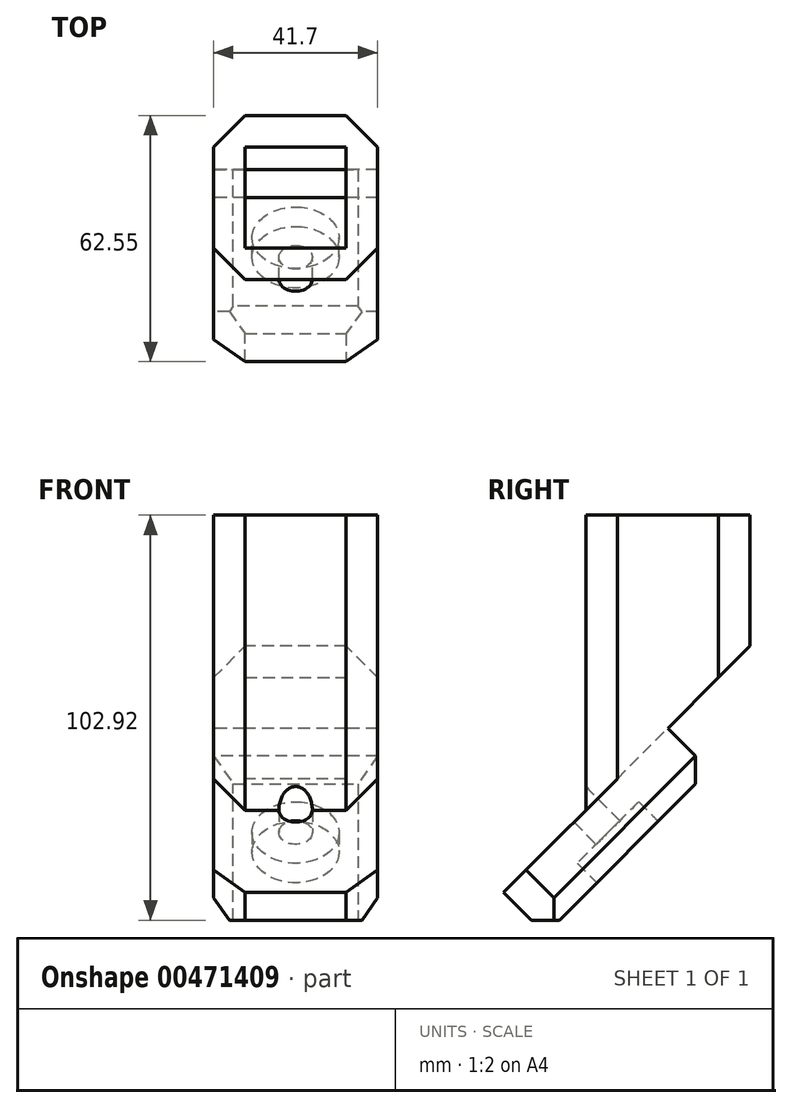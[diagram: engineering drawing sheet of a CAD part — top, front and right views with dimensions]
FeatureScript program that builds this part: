
annotation { "Feature Type Name" : "Feature", "Feature Type Description" : "" }
export const myFeature = defineFeature(function(context is Context, id is Id, definition is map)
    precondition{}
    {
        {
            var Q0;
            Q0=qCreatedBy(makeId("Top.planeOp"),FACE);
            var sketch = newSketch(context, id + "F0", { "sketchPlane" : qUnion([Q0])});
            skLineSegment(sketch, "E0", {"start": v(0, 0) * mm, "end": v(0, 12.85) * mm, "construction": true});
            skLineSegment(sketch, "E1", {"start": v(0, 12.85) * mm, "end": v(12.85, 12.85) * mm});
            skLineSegment(sketch, "E2", {"start": v(12.85, 12.85) * mm, "end": v(12.85, 0) * mm});
            skLineSegment(sketch, "E3", {"start": v(12.85, 0) * mm, "end": v(0, 0) * mm, "construction": true});
            skLineSegment(sketch, "E4", {"start": v(12.85, 0) * mm, "end": v(12.85, -12.85) * mm});
            skLineSegment(sketch, "E5", {"start": v(12.85, -12.85) * mm, "end": v(0, -12.85) * mm});
            skLineSegment(sketch, "E6", {"start": v(0, -12.85) * mm, "end": v(0, 0) * mm, "construction": true});
            skLineSegment(sketch, "E7", {"start": v(0, 0) * mm, "end": v(-12.85, 0) * mm, "construction": true});
            skLineSegment(sketch, "E8", {"start": v(-12.85, 0) * mm, "end": v(-12.85, 12.85) * mm});
            skLineSegment(sketch, "E9", {"start": v(-12.85, 12.85) * mm, "end": v(0, 12.85) * mm});
            skLineSegment(sketch, "E10", {"start": v(-12.85, 0) * mm, "end": v(-12.85, -12.85) * mm});
            skLineSegment(sketch, "E11", {"start": v(-12.85, -12.85) * mm, "end": v(0, -12.85) * mm});
            skLineSegment(sketch, "E12", {"start": v(0, 12.85) * mm, "end": v(0, 20.85) * mm, "construction": true});
            skLineSegment(sketch, "E13", {"start": v(0, 20.85) * mm, "end": v(20.85, 20.85) * mm});
            skLineSegment(sketch, "E14", {"start": v(20.85, 20.85) * mm, "end": v(20.85, 0) * mm});
            skLineSegment(sketch, "E15", {"start": v(20.85, 0) * mm, "end": v(12.85, 0) * mm, "construction": true});
            skLineSegment(sketch, "E16", {"start": v(20.85, 0) * mm, "end": v(20.85, -20.85) * mm});
            skLineSegment(sketch, "E17", {"start": v(20.85, -20.85) * mm, "end": v(0, -20.85) * mm});
            skLineSegment(sketch, "E18", {"start": v(0, -20.85) * mm, "end": v(0, -12.85) * mm, "construction": true});
            skLineSegment(sketch, "E19", {"start": v(0, -20.85) * mm, "end": v(-20.85, -20.85) * mm});
            skLineSegment(sketch, "E20", {"start": v(-20.85, -20.85) * mm, "end": v(-20.85, 0) * mm});
            skLineSegment(sketch, "E21", {"start": v(-20.85, 0) * mm, "end": v(-12.85, 0) * mm, "construction": true});
            skLineSegment(sketch, "E22", {"start": v(0, 20.85) * mm, "end": v(-20.85, 20.85) * mm});
            skLineSegment(sketch, "E23", {"start": v(-20.85, 20.85) * mm, "end": v(-20.85, 0) * mm});
            skSolve(sketch);
        }
        {
            var Q0;
            Q0 = qSketchRegion(id + "F0", true);
            extrude(context, id + "F1", {"entities" : qUnion([Q0]), "depth" : 75 * mm});
        }
        {
            var Q0;
            Q0=makeQuery(id+"F1.opExtrude","SWEPT_FACE",FACE,{"disambiguationData":[OSD([sQuery(id+"F0.wireOp",EDGE,"E20"),sQuery(id+"F0.wireOp",EDGE,"E23")])]});
            var sketch = newSketch(context, id + "F2", { "sketchPlane" : qUnion([Q0])});
            skLineSegment(sketch, "E24", {"start": v(20.85, 0) * mm, "end": v(-20.85, 41.7) * mm});
            skLineSegment(sketch, "E25", {"start": v(-20.85, 41.7) * mm, "end": v(-20.85, 0) * mm});
            skLineSegment(sketch, "E26", {"start": v(-20.85, 0) * mm, "end": v(20.85, 0) * mm});
            skSolve(sketch);
        }
        {
            var Q0;
            Q0 = qSketchRegion(id + "F2", true);
            extrude(context, id + "F3", {"entities" : qUnion([Q0]), "operationType" : NewBodyOperationType.REMOVE, "endBound" : BoundingType.THROUGH_ALL, "oppositeDirection" : true, "depth" : 25 * mm});
        }
        {
            var Q0;
            Q0=makeQuery(id+"F3.boolean.opBoolean","COPY",FACE,{"derivedFrom":makeQuery(id+"F3.opExtrude","SWEPT_FACE",FACE,{"disambiguationData":[OSD([sQuery(id+"F2.wireOp",EDGE,"E24")])]})});
            var sketch = newSketch(context, id + "F4", { "sketchPlane" : qUnion([Q0])});
            skPoint(sketch, "E27.centerSnap0", {"position": v(12.85, -14.74) * mm});
            skLineSegment(sketch, "E28", {"start": v(20.85, -44.23) * mm, "end": v(-20.85, -44.23) * mm});
            skLineSegment(sketch, "E29", {"start": v(-20.85, -44.23) * mm, "end": v(-20.85, 14.74) * mm});
            skLineSegment(sketch, "E30", {"start": v(-20.85, 14.74) * mm, "end": v(20.85, 14.74) * mm});
            skLineSegment(sketch, "E31", {"start": v(20.85, 14.74) * mm, "end": v(20.85, -44.23) * mm});
            skSolve(sketch);
        }
        {
            var Q0;
            Q0 = qSketchRegion(id + "F4", true);
            extrude(context, id + "F5", {"entities" : qUnion([Q0]), "operationType" : NewBodyOperationType.ADD, "depth" : 15 * mm});
        }
        {
            var Q0;
            Q0=makeQuery(id+"F5.opExtrude","CAP_FACE",FACE,{"disambiguationData":[OSD([sQuery(id+"F4.wireOp",EDGE,"E28"),sQuery(id+"F4.wireOp",EDGE,"E29"),sQuery(id+"F4.wireOp",EDGE,"E30"),sQuery(id+"F4.wireOp",EDGE,"E31")])],"isStart":false});
            var sketch = newSketch(context, id + "F6", { "sketchPlane" : qUnion([Q0])});
            skLineSegment(sketch, "E32", {"start": v(0, -44.23) * mm, "end": v(0, -14.74) * mm, "construction": true});
            skPoint(sketch, "E32.endSnap0", {"position": v(20.85, -14.74) * mm});
            skLineSegment(sketch, "E33", {"start": v(0, -14.74) * mm, "end": v(20.85, -14.74) * mm, "construction": true});
            skCircle(sketch, "E34", {"center": v(0, -14.74) * mm, "radius": 11.05 * mm});
            skSolve(sketch);
        }
        {
            var Q0;
            Q0 = qSketchRegion(id + "F6", true);
            extrude(context, id + "F7", {"entities" : qUnion([Q0]), "operationType" : NewBodyOperationType.REMOVE, "oppositeDirection" : true, "depth" : 7 * mm});
        }
        {
            var Q0;
            Q0=makeQuery(id+"F7.boolean.opBoolean","COPY",FACE,{"derivedFrom":makeQuery(id+"F7.opExtrude","CAP_FACE",FACE,{"disambiguationData":[OSD([sQuery(id+"F6.wireOp",EDGE,"E34")])],"isStart":false})});
            var sketch = newSketch(context, id + "F8", { "sketchPlane" : qUnion([Q0])});
            skCircle(sketch, "E35", {"center": v(0, -14.74) * mm, "radius": 4.25 * mm});
            skSolve(sketch);
        }
        {
            var Q0;
            Q0 = qSketchRegion(id + "F8", true);
            extrude(context, id + "F9", {"entities" : qUnion([Q0]), "operationType" : NewBodyOperationType.REMOVE, "endBound" : BoundingType.THROUGH_ALL, "oppositeDirection" : true, "depth" : 25 * mm});
        }
        {
            var Q0;
            Q0=makeQuery(id+"F1.opExtrude","SWEPT_EDGE",EDGE,{"disambiguationData":[OSD([sQuery(id+"F0.wireOp",EDGE,"E19"),sQuery(id+"F0.wireOp",EDGE,"E20")])]});
            var Q1;
            Q1=makeQuery(id+"F1.opExtrude","SWEPT_EDGE",EDGE,{"disambiguationData":[OSD([sQuery(id+"F0.wireOp",EDGE,"E16"),sQuery(id+"F0.wireOp",EDGE,"E17")])]});
            var Q2;
            Q2=makeQuery(id+"F1.opExtrude","SWEPT_EDGE",EDGE,{"disambiguationData":[OSD([sQuery(id+"F0.wireOp",EDGE,"E13"),sQuery(id+"F0.wireOp",EDGE,"E14")])]});
            var Q3;
            Q3=makeQuery(id+"F1.opExtrude","SWEPT_EDGE",EDGE,{"disambiguationData":[OSD([sQuery(id+"F0.wireOp",EDGE,"E22"),sQuery(id+"F0.wireOp",EDGE,"E23")])]});
            chamfer(context, id + "F10", {"entities" : qUnion([Q0, Q1, Q2, Q3]), "width" : 8 * mm, "tangentPropagation" : true});
        }
        {
            var Q0;
            Q0=makeQuery(id+"F5.opExtrude","CAP_FACE",FACE,{"disambiguationData":[OSD([sQuery(id+"F4.wireOp",EDGE,"E28"),sQuery(id+"F4.wireOp",EDGE,"E29"),sQuery(id+"F4.wireOp",EDGE,"E30"),sQuery(id+"F4.wireOp",EDGE,"E31")])],"isStart":false});
            cPlane(context, id + "F11", {"entities" : qUnion([Q0]), "cplaneType" : CPlaneType.OFFSET, "offset" : 55 * mm, "oppositeDirection" : true, "width" : 150 * mm, "height" : 150 * mm});
        }
        {
            var Q0;
            Q0=makeQuery(id+"F5.opExtrude","CAP_EDGE",EDGE,{"disambiguationData":[OSD([sQuery(id+"F4.wireOp",EDGE,"E30")])],"isStart":false});
            var Q1;
            Q1=makeQuery(id+"F5.opExtrude","CAP_EDGE",EDGE,{"disambiguationData":[OSD([sQuery(id+"F4.wireOp",EDGE,"E29")])],"isStart":false});
            var Q2;
            Q2=makeQuery(id+"F5.opExtrude","CAP_EDGE",EDGE,{"disambiguationData":[OSD([sQuery(id+"F4.wireOp",EDGE,"E31")])],"isStart":false});
            var Q3;
            Q3=makeQuery(id+"F5.opExtrude","CAP_EDGE",EDGE,{"disambiguationData":[OSD([sQuery(id+"F4.wireOp",EDGE,"E28")])],"isStart":false});
            chamfer(context, id + "F12", {"entities" : qUnion([Q0, Q1, Q2, Q3]), "width" : 5 * mm, "tangentPropagation" : true});
        }
        {
            var Q0;
            Q0=makeQuery(id+"F5.opExtrude","SWEPT_EDGE",EDGE,{"disambiguationData":[OSD([sQuery(id+"F4.wireOp",EDGE,"E28"),sQuery(id+"F4.wireOp",EDGE,"E31")])]});
            var Q1;
            Q1=makeQuery(id+"F5.opExtrude","SWEPT_EDGE",EDGE,{"disambiguationData":[OSD([sQuery(id+"F4.wireOp",EDGE,"E28"),sQuery(id+"F4.wireOp",EDGE,"E29")])]});
            chamfer(context, id + "F13", {"entities" : qUnion([Q0, Q1]), "width" : 8 * mm, "tangentPropagation" : true});
        }
    });
